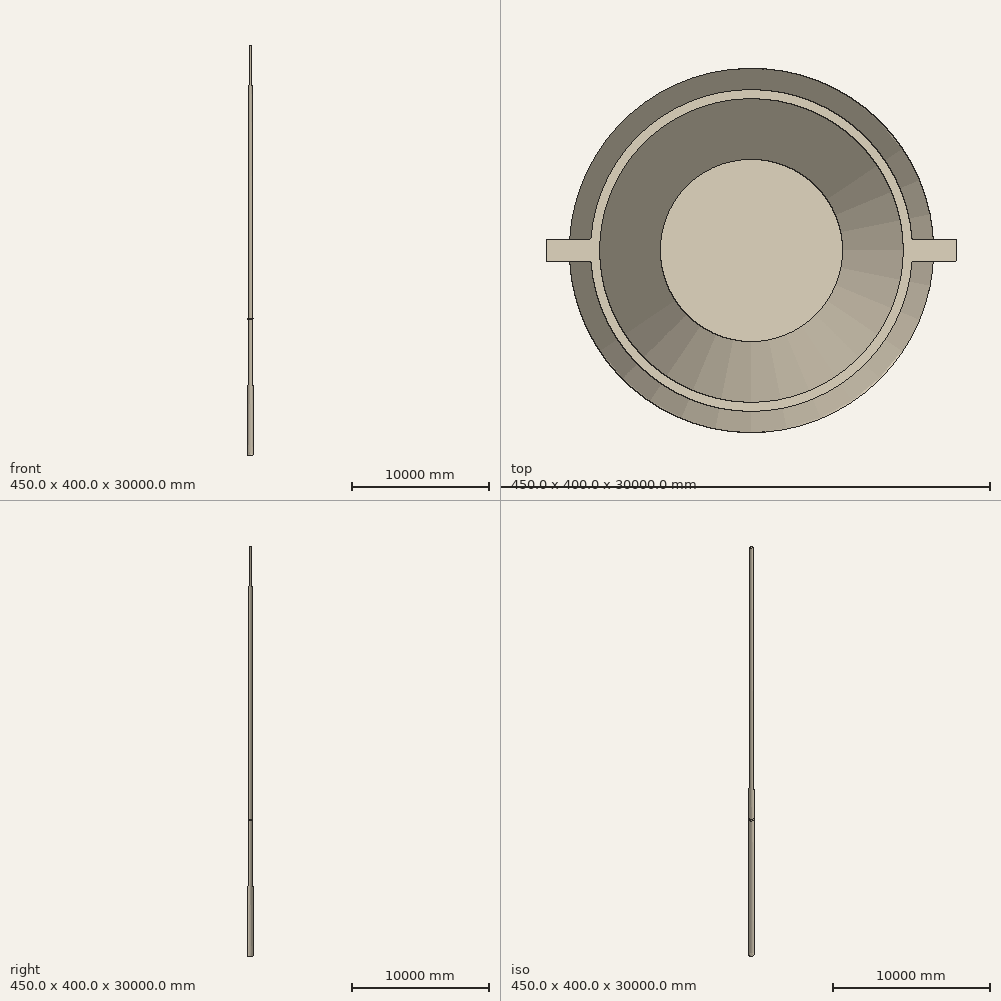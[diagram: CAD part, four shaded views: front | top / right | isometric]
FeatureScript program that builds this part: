
annotation { "Feature Type Name" : "Feature", "Feature Type Description" : "" }
export const myFeature = defineFeature(function(context is Context, id is Id, definition is map)
    precondition{}
    {
        {
            var Q0;
            Q0=qCreatedBy(makeId("Top.planeOp"),FACE);
            var sketch = newSketch(context, id + "F0", { "sketchPlane" : qUnion([Q0])});
            skCircle(sketch, "E0", {"center": v(0, 0) * mm, "radius": 200 * mm});
            skSolve(sketch);
        }
        {
            var Q0;
            Q0=qCreatedBy(makeId("Top.planeOp"),FACE);
            cPlane(context, id + "F1", {"entities" : qUnion([Q0]), "cplaneType" : CPlaneType.OFFSET, "offset" : 30000 * mm, "width" : 150 * mm, "height" : 150 * mm});
        }
        {
            var Q0;
            Q0=qCreatedBy(id+"F1.planeOp",FACE);
            var sketch = newSketch(context, id + "F2", { "sketchPlane" : qUnion([Q0])});
            skCircle(sketch, "E1", {"center": v(0, 0) * mm, "radius": 100 * mm});
            skSolve(sketch);
        }
        {
            var Q0;
            Q0=makeQuery(id+"F2.imprint","IMPRINT",FACE,{"disambiguationData":[TD([[makeQuery(id+"F2.imprint","IMPRINT",EDGE,{"derivedFrom":sQuery(id+"F2.wireOp",EDGE,"E1")}),1.0]])]});
            var Q1;
            Q1=makeQuery(id+"F0.imprint","IMPRINT",FACE,{"disambiguationData":[TD([[makeQuery(id+"F0.imprint","IMPRINT",EDGE,{"derivedFrom":sQuery(id+"F0.wireOp",EDGE,"E0")}),1.0]])]});
            loft(context, id + "F3", {"sheetProfilesArray" : [{ "sheetProfileEntities" : qUnion([Q0]) }, { "sheetProfileEntities" : qUnion([Q1]) }]});
        }
        {
            var Q0;
            Q0=qCreatedBy(makeId("Front.planeOp"),FACE);
            var sketch = newSketch(context, id + "F4", { "sketchPlane" : qUnion([Q0])});
            skCircle(sketch, "E2", {"center": v(0, 100) * mm, "radius": 20 * mm});
            skSolve(sketch);
        }
        {
            var Q0;
            Q0 = qSketchRegion(id + "F4", true);
            extrude(context, id + "F5", {"entities" : qUnion([Q0]), "operationType" : NewBodyOperationType.REMOVE, "endBound" : BoundingType.THROUGH_ALL, "oppositeDirection" : true, "depth" : 25 * mm, "offsetDistance" : 25 * mm, "hasSecondDirection" : true, "secondDirectionBound" : SecondDirectionBoundingType.THROUGH_ALL, "secondDirectionOppositeDirection" : false, "secondDirectionDepth" : 25 * mm});
        }
        {
            var Q0;
            Q0=qCreatedBy(makeId("Top.planeOp"),FACE);
            cPlane(context, id + "F6", {"entities" : qUnion([Q0]), "cplaneType" : CPlaneType.OFFSET, "offset" : 10000 * mm, "width" : 150 * mm, "height" : 150 * mm});
        }
        {
            var Q0;
            Q0=qCreatedBy(id+"F6.planeOp",FACE);
            var sketch = newSketch(context, id + "F7", { "sketchPlane" : qUnion([Q0])});
            skCircle(sketch, "E3", {"center": v(0, 0) * mm, "radius": 166.67 * mm});
            skLineSegment(sketch, "E4.bottom", {"start": v(225, 12.5) * mm, "end": v(225, -12.5) * mm});
            skLineSegment(sketch, "E4.top", {"start": v(-225, 12.5) * mm, "end": v(-225, -12.5) * mm});
            skLineSegment(sketch, "E4.left", {"start": v(225, 12.5) * mm, "end": v(176.22, 12.5) * mm});
            skLineSegment(sketch, "E4.right", {"start": v(225, -12.5) * mm, "end": v(176.22, -12.5) * mm});
            skArc(sketch, "E5.0", {"start": v(176.22, 12.5) * mm, "mid": v(0, 176.67) * mm, "end": v(-176.22, 12.5) * mm});
            skLineSegment(sketch, "E6.trimOffspring", {"start": v(-176.22, 12.5) * mm, "end": v(-225, 12.5) * mm});
            skLineSegment(sketch, "E7.trimOffspring", {"start": v(-176.22, -12.5) * mm, "end": v(-225, -12.5) * mm});
            skArc(sketch, "E8.trimOffspring", {"start": v(-176.22, -12.5) * mm, "mid": v(0, -176.67) * mm, "end": v(176.22, -12.5) * mm});
            skLineSegment(sketch, "E9", {"start": v(-225, 0) * mm, "end": v(225, 0) * mm, "construction": true});
            skSolve(sketch);
        }
        {
            var Q0;
            Q0 = qSketchRegion(id + "F7", true);
            extrude(context, id + "F8", {"entities" : qUnion([Q0]), "endBound" : BoundingType.SYMMETRIC, "depth" : 100 * mm, "offsetDistance" : 25 * mm});
        }
        {
            var Q0;
            Q0=qCreatedBy(makeId("Front.planeOp"),FACE);
            var sketch = newSketch(context, id + "F9", { "sketchPlane" : qUnion([Q0])});
            skCircle(sketch, "E10", {"center": v(200, 10000) * mm, "radius": 15 * mm});
            skCircle(sketch, "E11", {"center": v(-200, 10000) * mm, "radius": 15 * mm});
            skSolve(sketch);
        }
        {
            var Q0;
            Q0 = qSketchRegion(id + "F9", true);
            extrude(context, id + "F10", {"entities" : qUnion([Q0]), "operationType" : NewBodyOperationType.REMOVE, "endBound" : BoundingType.THROUGH_ALL, "oppositeDirection" : true, "depth" : 25 * mm, "offsetDistance" : 25 * mm, "hasSecondDirection" : true, "secondDirectionBound" : SecondDirectionBoundingType.THROUGH_ALL, "secondDirectionOppositeDirection" : false, "secondDirectionDepth" : 25 * mm});
        }
    });
